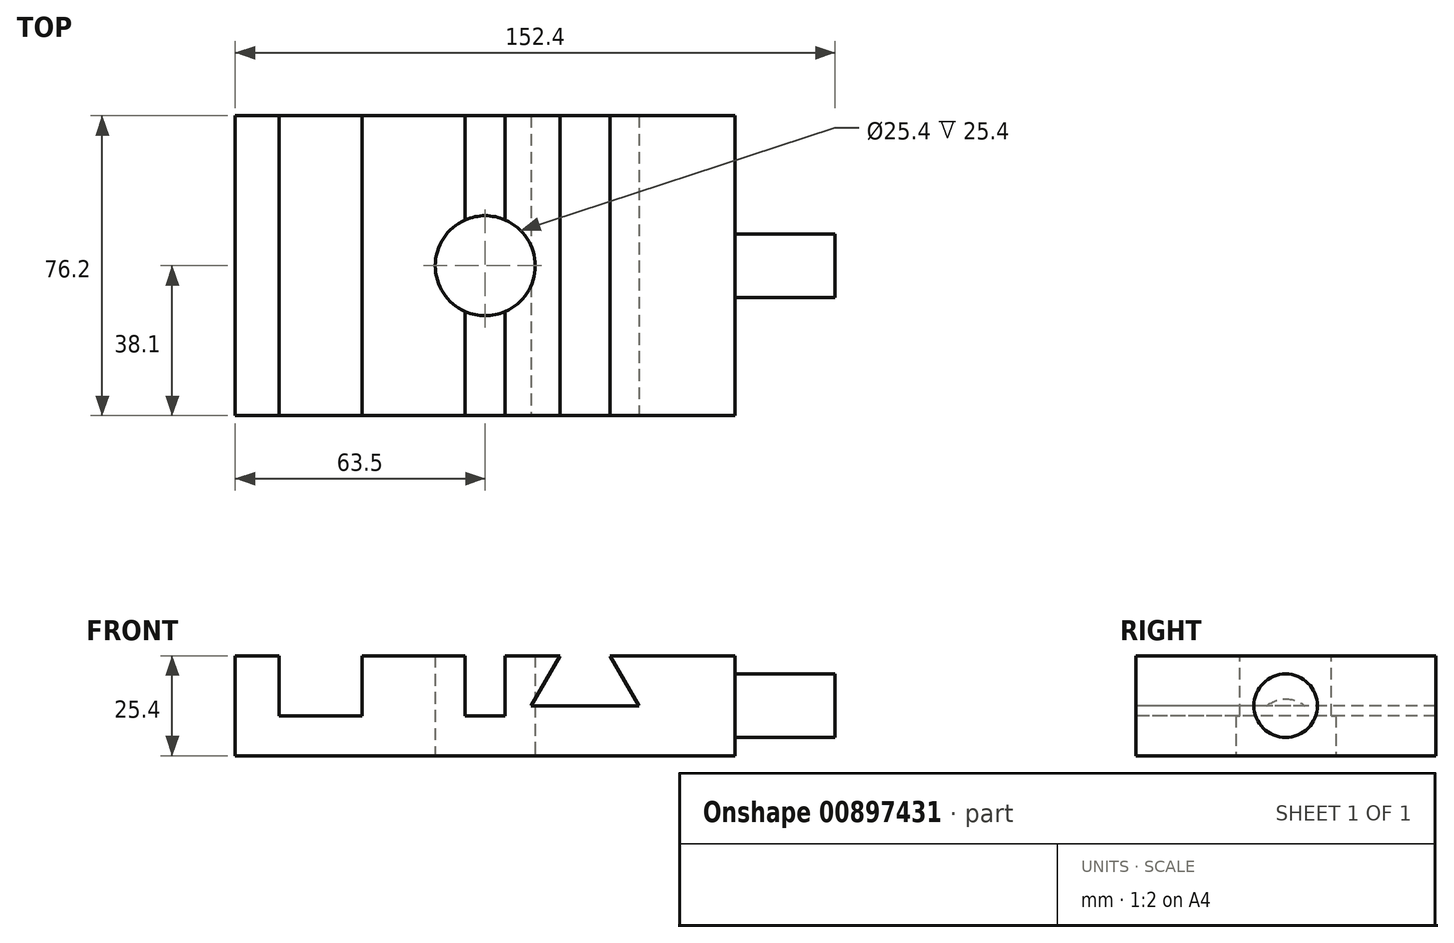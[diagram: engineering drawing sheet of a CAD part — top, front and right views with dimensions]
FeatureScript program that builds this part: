
annotation { "Feature Type Name" : "Feature", "Feature Type Description" : "" }
export const myFeature = defineFeature(function(context is Context, id is Id, definition is map)
    precondition{}
    {
        {
            var Q0;
            Q0=qCreatedBy(makeId("Top.planeOp"),FACE);
            var sketch = newSketch(context, id + "F0", { "sketchPlane" : qUnion([Q0])});
            skLineSegment(sketch, "E0.bottom", {"start": v(63.5, 38.1) * mm, "end": v(-63.5, 38.1) * mm});
            skLineSegment(sketch, "E0.top", {"start": v(63.5, -38.1) * mm, "end": v(-63.5, -38.1) * mm});
            skLineSegment(sketch, "E0.left", {"start": v(63.5, 38.1) * mm, "end": v(63.5, -38.1) * mm});
            skLineSegment(sketch, "E0.right", {"start": v(-63.5, 38.1) * mm, "end": v(-63.5, -38.1) * mm});
            skPoint(sketch, "E0.middle", {"position": v(0, 0) * mm});
            skCircle(sketch, "E1", {"center": v(0, 0) * mm, "radius": 12.7 * mm});
            skSolve(sketch);
        }
        {
            var Q0;
            Q0=makeQuery(id+"F0.imprint","IMPRINT",FACE,{"disambiguationData":[TD([[makeQuery(id+"F0.imprint","IMPRINT",EDGE,{"derivedFrom":sQuery(id+"F0.wireOp",EDGE,"E0.bottom")}),1.0]])]});
            var sketch = newSketch(context, id + "F1", { "sketchPlane" : qUnion([Q0])});
            skSolve(sketch);
        }
        {
            var Q0;
            Q0=makeQuery(id+"F1.imprint","IMPRINT",FACE,{"disambiguationData":[TD([[makeQuery(id+"F1.imprint","IMPRINT",EDGE,{"derivedFrom":makeQuery(id+"F0.imprint","IMPRINT",EDGE,{"derivedFrom":sQuery(id+"F0.wireOp",EDGE,"E0.bottom")})}),1.0]])]});
            extrude(context, id + "F2", {"entities" : qUnion([Q0]), "depth" : 25.4 * mm, "offsetDistance" : 25.4 * mm});
        }
        {
            var Q0;
            Q0=makeQuery(id+"F2.opExtrude","CAP_FACE",FACE,{"disambiguationData":[OSD([sQuery(id+"F0.wireOp",EDGE,"E0.bottom"),sQuery(id+"F0.wireOp",EDGE,"E0.top"),sQuery(id+"F0.wireOp",EDGE,"E0.left"),sQuery(id+"F0.wireOp",EDGE,"E0.right"),sQuery(id+"F0.wireOp",EDGE,"E1")])],"isStart":false});
            var sketch = newSketch(context, id + "F3", { "sketchPlane" : qUnion([Q0])});
            skLineSegment(sketch, "E2.bottom", {"start": v(-52.32, 38.1) * mm, "end": v(-31.24, 38.1) * mm});
            skLineSegment(sketch, "E2.top", {"start": v(-52.32, -38.1) * mm, "end": v(-31.24, -38.1) * mm});
            skLineSegment(sketch, "E2.left", {"start": v(-52.32, 38.1) * mm, "end": v(-52.32, -38.1) * mm});
            skLineSegment(sketch, "E2.right", {"start": v(-31.24, 38.1) * mm, "end": v(-31.24, -38.1) * mm});
            skLineSegment(sketch, "E3", {"start": v(-5.1, 38.1) * mm, "end": v(-5.1, -38.1) * mm});
            skLineSegment(sketch, "E4", {"start": v(5.07, 38.1) * mm, "end": v(5.07, -38.1) * mm});
            skPoint(sketch, "E5", {"position": v(0, 0) * mm});
            skLineSegment(sketch, "E6", {"start": v(0, 38.1) * mm, "end": v(0, -38.1) * mm, "construction": true});
            skSolve(sketch);
        }
        {
            var Q0;
            Q0=makeQuery(id+"F3.imprint","IMPRINT",FACE,{"disambiguationData":[TD([[makeQuery(id+"F3.imprint","IMPRINT",EDGE,{"derivedFrom":sQuery(id+"F3.wireOp",EDGE,"E2.bottom")}),1.0]])]});
            var Q1;
            {var subQ0=sQuery(id+"F3.wireOp",EDGE,"E3");var subQ1=makeQuery(id+"F2.opExtrude","CAP_EDGE",EDGE,{"disambiguationData":[OSD([sQuery(id+"F0.wireOp",EDGE,"E0.bottom")])],"isStart":false});var subQ2=makeQuery(id+"F3.imprint","INTERSECT",VERTEX,{"derivedFrom":[subQ1,subQ0]});Q1=makeQuery(id+"F3.imprint","IMPRINT",FACE,{"disambiguationData":[TD([[makeQuery(id+"F3.imprint","IMPRINT",EDGE,{"disambiguationData":[TD([[subQ2,-1.0]])],"derivedFrom":subQ0}),1.0]])]});}
            var Q2;
            {var subQ0=sQuery(id+"F3.wireOp",EDGE,"E3");var subQ1=makeQuery(id+"F2.opExtrude","CAP_EDGE",EDGE,{"disambiguationData":[OSD([sQuery(id+"F0.wireOp",EDGE,"E0.top")])],"isStart":false});var subQ2=makeQuery(id+"F3.imprint","INTERSECT",VERTEX,{"derivedFrom":[subQ1,subQ0]});Q2=makeQuery(id+"F3.imprint","IMPRINT",FACE,{"disambiguationData":[TD([[makeQuery(id+"F3.imprint","IMPRINT",EDGE,{"disambiguationData":[TD([[subQ2,1.0]])],"derivedFrom":subQ0}),1.0]])]});}
            extrude(context, id + "F4", {"entities" : qUnion([Q0, Q1, Q2]), "operationType" : NewBodyOperationType.REMOVE, "oppositeDirection" : true, "depth" : 15.24 * mm, "offsetDistance" : 25.4 * mm});
        }
        {
            var Q0;
            Q0=makeQuery(id+"F2.opExtrude","SWEPT_FACE",FACE,{"disambiguationData":[OSD([sQuery(id+"F0.wireOp",EDGE,"E0.top")])]});
            var sketch = newSketch(context, id + "F5", { "sketchPlane" : qUnion([Q0])});
            skLineSegment(sketch, "E7", {"start": v(19.04, 25.4) * mm, "end": v(11.7, 12.7) * mm});
            skLineSegment(sketch, "E8", {"start": v(11.7, 12.7) * mm, "end": v(39.07, 12.7) * mm});
            skLineSegment(sketch, "E9", {"start": v(39.07, 12.7) * mm, "end": v(31.74, 25.4) * mm});
            skLineSegment(sketch, "E10", {"start": v(31.74, 25.4) * mm, "end": v(19.04, 25.4) * mm});
            skLineSegment(sketch, "E11", {"start": v(25.39, 12.7) * mm, "end": v(25.39, 25.4) * mm, "construction": true});
            skSolve(sketch);
        }
        {
            var Q0;
            Q0=makeQuery(id+"F5.imprint","IMPRINT",FACE,{"disambiguationData":[TD([[makeQuery(id+"F5.imprint","IMPRINT",EDGE,{"derivedFrom":sQuery(id+"F5.wireOp",EDGE,"E7")}),1.0]])]});
            extrude(context, id + "F6", {"entities" : qUnion([Q0]), "operationType" : NewBodyOperationType.REMOVE, "endBound" : BoundingType.THROUGH_ALL, "oppositeDirection" : true, "depth" : 25.4 * mm, "offsetDistance" : 25.4 * mm});
        }
        {
            var Q0;
            Q0=makeQuery(id+"F2.opExtrude","SWEPT_FACE",FACE,{"disambiguationData":[OSD([sQuery(id+"F0.wireOp",EDGE,"E0.left")])]});
            var sketch = newSketch(context, id + "F7", { "sketchPlane" : qUnion([Q0])});
            skCircle(sketch, "E12", {"center": v(0, 12.7) * mm, "radius": 8.06 * mm});
            skPoint(sketch, "E12.centerSnap0", {"position": v(-38.1, 12.7) * mm});
            skPoint(sketch, "E12.centerSnap1", {"position": v(0, 25.4) * mm});
            skSolve(sketch);
        }
        {
            var Q0;
            Q0=makeQuery(id+"F7.imprint","IMPRINT",FACE,{"disambiguationData":[TD([[makeQuery(id+"F7.imprint","IMPRINT",EDGE,{"derivedFrom":sQuery(id+"F7.wireOp",EDGE,"E12")}),1.0]])]});
            extrude(context, id + "F8", {"entities" : qUnion([Q0]), "operationType" : NewBodyOperationType.ADD, "depth" : 25.4 * mm, "offsetDistance" : 25.4 * mm});
        }
    });
